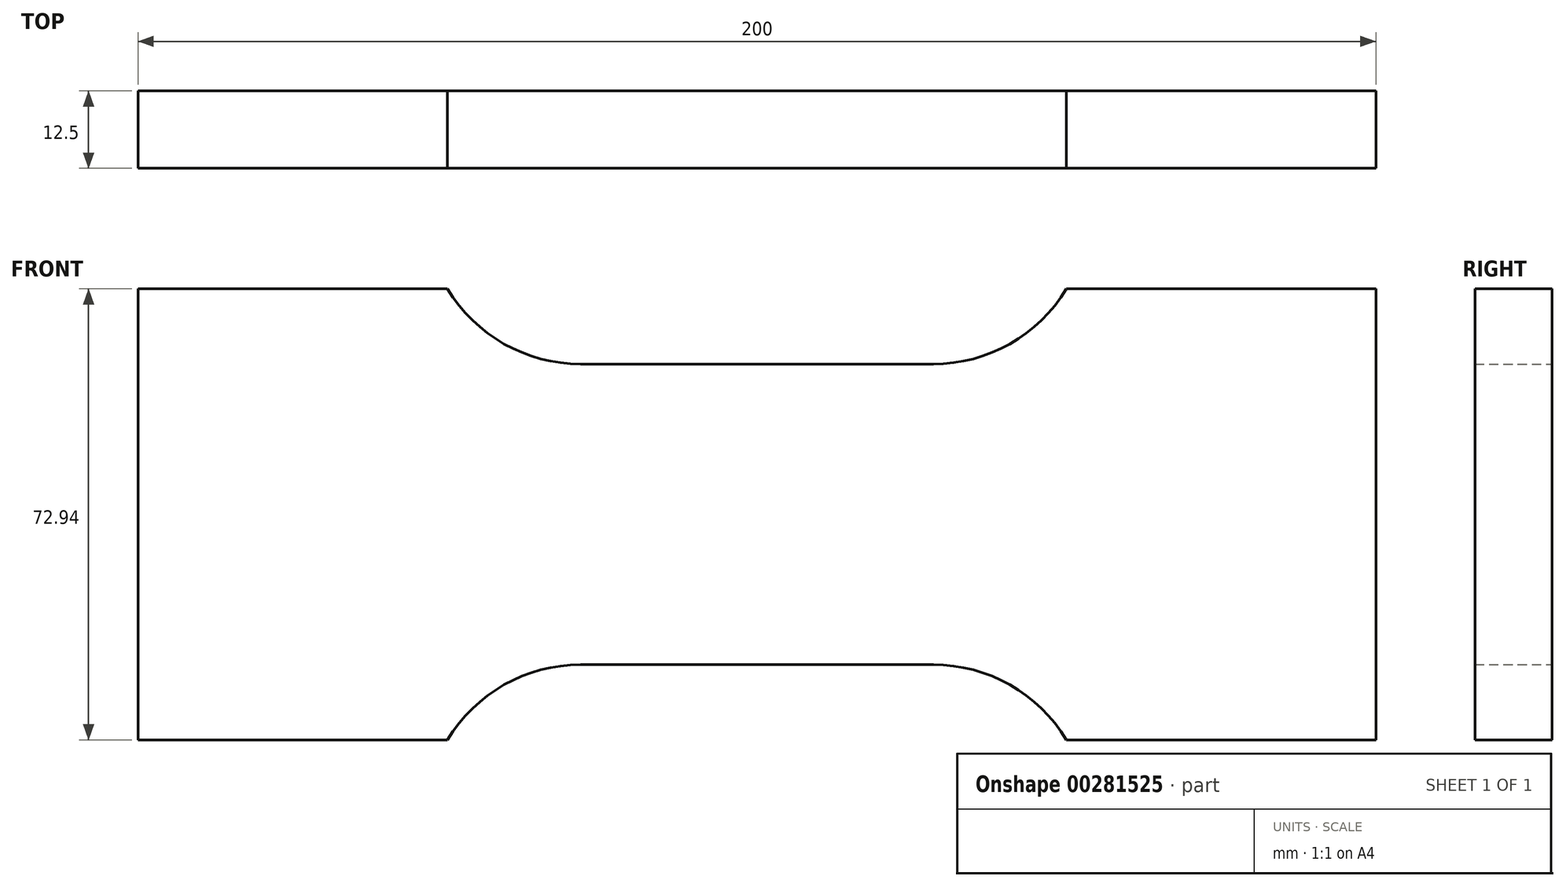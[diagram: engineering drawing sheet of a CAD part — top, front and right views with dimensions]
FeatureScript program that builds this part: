
annotation { "Feature Type Name" : "Feature", "Feature Type Description" : "" }
export const myFeature = defineFeature(function(context is Context, id is Id, definition is map)
    precondition{}
    {
        {
            var Q0;
            Q0=qCreatedBy(makeId("Front.planeOp"),FACE);
            var sketch = newSketch(context, id + "F0", { "sketchPlane" : qUnion([Q0])});
            skLineSegment(sketch, "E0", {"start": v(0, 24.3) * mm, "end": v(28.5, 24.3) * mm});
            skArc(sketch, "E1", {"start": v(28.5, 24.3) * mm, "mid": v(40.85, 27.56) * mm, "end": v(50, 36.47) * mm});
            skLineSegment(sketch, "E2", {"start": v(50, 36.47) * mm, "end": v(100, 36.47) * mm});
            skLineSegment(sketch, "E3", {"start": v(100, 0) * mm, "end": v(100, 36.47) * mm});
            skLineSegment(sketch, "E4.MirrorCS", {"start": v(0, -24.3) * mm, "end": v(28.5, -24.3) * mm});
            skLineSegment(sketch, "E5.MirrorCS", {"start": v(100, 0) * mm, "end": v(100, -36.47) * mm});
            skLineSegment(sketch, "E6.MirrorCS", {"start": v(50, -36.47) * mm, "end": v(100, -36.47) * mm});
            skArc(sketch, "E7.MirrorCS", {"start": v(28.5, -24.3) * mm, "mid": v(40.85, -27.56) * mm, "end": v(50, -36.47) * mm});
            skArc(sketch, "E8.MirrorCS", {"start": v(-28.5, -24.3) * mm, "mid": v(-40.85, -27.56) * mm, "end": v(-50, -36.47) * mm});
            skLineSegment(sketch, "E9.MirrorCS", {"start": v(-50, -36.47) * mm, "end": v(-100, -36.47) * mm});
            skArc(sketch, "E10.MirrorCS", {"start": v(-28.5, 24.3) * mm, "mid": v(-40.85, 27.56) * mm, "end": v(-50, 36.47) * mm});
            skLineSegment(sketch, "E11.MirrorCS", {"start": v(-50, 36.47) * mm, "end": v(-100, 36.47) * mm});
            skLineSegment(sketch, "E12.MirrorCS", {"start": v(-100, 0) * mm, "end": v(-100, -36.47) * mm});
            skLineSegment(sketch, "E13.MirrorCS", {"start": v(0, -24.3) * mm, "end": v(-28.5, -24.3) * mm});
            skLineSegment(sketch, "E14.MirrorCS", {"start": v(-100, 0) * mm, "end": v(-100, 36.47) * mm});
            skLineSegment(sketch, "E15.MirrorCS", {"start": v(0, 24.3) * mm, "end": v(-28.5, 24.3) * mm});
            skSolve(sketch);
        }
        {
            var Q0;
            Q0=makeQuery(id+"F0.imprint","IMPRINT",FACE,{"disambiguationData":[TD([[makeQuery(id+"F0.imprint","IMPRINT",EDGE,{"derivedFrom":sQuery(id+"F0.wireOp",EDGE,"E0")}),-1.0]])]});
            extrude(context, id + "F1", {"entities" : qUnion([Q0]), "endBound" : BoundingType.SYMMETRIC, "depth" : 12.5 * mm});
        }
    });
